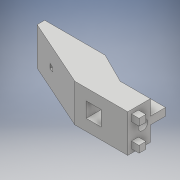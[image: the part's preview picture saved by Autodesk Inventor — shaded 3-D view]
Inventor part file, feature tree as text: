
AUTODESK INVENTOR PART (.ipt)
format: ipt  version: 2017 (Build 210142000, 142)  size: 209,408 bytes
history: native  units: mm
features: sketch x13, extrude x12, hole x1, chamfer x1
ambient origin geometry x8: Origin, YZ Plane, XZ Plane, XY Plane, X Axis, Y Axis, Z Axis, Center Point
bodies: Solid1 (feature_tree)
feature tree (27):
  extrude  "Extrusion1"  Depth=25.0mm
  sketch  "Sketch2"  dims[d2=80.0mm d3=0.0mm d4=2.5mm]
  extrude  "Extrusion2"  Depth=2.5mm
  extrude  "Extrusion3"  Depth=2.5mm
  extrude  "Extrusion4"  Depth=80.0mm TaperAngle=0.0deg
  extrude  "Extrusion5"  Depth=10.0mm TaperAngle=0.0deg
  extrude  "Extrusion6"  Depth=10.0mm TaperAngle=0.0deg
  extrude  "Extrusion7"  Depth=20.0mm
  extrude  "Extrusion15"  Depth=20.0mm
  extrude  "Extrusion18"  Depth=25.0mm TaperAngle=0.0deg
  hole  "Hole1"  [1 undecoded]
  extrude  "Extrusion19"  Depth=10.0mm
  chamfer  "Chamfer3"  Distance=10.0mm
  extrude  "Extrusion20"  Depth=2.8mm
  extrude  "Extrusion21"  Depth=2.8mm
  sketch  "Sketch1"  dims[d0=15.0mm d1=25.0mm]
  sketch  "Sketch4"  dims[d5=10.0mm d6=2.5mm]
  sketch  "Sketch5"  dims[d7=10.0mm d10=80.0mm d11=0.0mm]
  sketch  "Sketch6"  dims[d12=40.0mm d13=10.0mm d14=0.0mm]
  sketch  "Sketch7"  dims[d15=20.0mm d16=10.0mm d17=0.0mm]
  sketch  "Sketch8"  dims[d18=10.0mm d19=0.0mm d20=20.0mm]
  sketch  "Sketch21"  dims[d21=10.0mm d22=0.0mm d23=20.0mm]
  sketch  "Sketch28"  dims[d24=45.0mm d25=25.0mm d26=0.0mm]
  sketch  "Sketch30"  dims[d63=1.2mm d64=1.2mm]
  sketch  "Sketch31"  dims[d65=8.2mm d66=0.0mm d86=10.0mm]
  sketch  "Sketch32"  dims[d87=10.0mm d88=10.0mm d89=0.0mm]
  sketch  "Sketch33"  dims[d90=10.0mm d91=6.4mm d92=6.0mm d93=4.0mm d94=2.0mm d95=90.0deg d96=10.0mm d97=20.594885mm d98=2.8mm d99=2.8mm d100=10.0mm d101=0.0mm d102=0.8mm d103=2.0mm d104=45.0deg d105=2.5mm d106=2.5mm d107=4.5mm d108=4.5mm d109=5.0mm d110=0.0mm d111=2.5mm d112=2.5mm d113=4.5mm d114=4.5mm d115=5.0mm d116=0.0mm]
note: 1 required parameter value undecoded (feature->parameter linkage not recoverable at this tier; creation-order binding heuristic only, values carry confidence <= 0.55)
